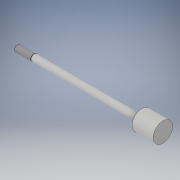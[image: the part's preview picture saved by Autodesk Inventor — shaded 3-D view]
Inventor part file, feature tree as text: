
AUTODESK INVENTOR PART (.ipt)
format: ipt  version: 2019 (Build 230136000, 136)  size: 162,304 bytes
history: native  units: in
note: dims shown in document units (in); Inventor stores cm internally (conversion verified against a paired STEP export)
features: other x70, revolve x3, sketch x3, thread x1
ambient origin geometry x8: Origin, YZ Plane, XZ Plane, XY Plane, X Axis, Y Axis, Z Axis, Center Point
bodies: Solid1 (feature_tree)
feature tree (77):
  revolve  "Revolution1"  Angle=360.0deg
  revolve  "Revolution2"  Angle=360.0deg
  thread  "Thread1"  [1 undecoded]
  revolve  "Revolution3"  [1 undecoded]
  other  "dia1_XY"
  other  "dia1_YZ"
  other  "dia1_ZX"
  other  "dia1_X"
  other  "dia1_Y"
  other  "dia1_Z"
  other  "dia1_Center"
  other  "dia12_XY"
  other  "dia12_YZ"
  other  "dia12_ZX"
  other  "dia12_X"
  other  "dia12_Y"
  other  "dia12_Z"
  other  "dia12_Center"
  other  "dia2_XY"
  other  "dia2_YZ"
  other  "dia2_ZX"
  other  "dia2_X"
  other  "dia2_Y"
  other  "dia2_Z"
  other  "dia2_Center"
  other  "dia22_XY"
  other  "dia22_YZ"
  other  "dia22_ZX"
  other  "dia22_X"
  other  "dia22_Y"
  other  "dia22_Z"
  other  "dia22_Center"
  other  "rl1_XY"
  other  "rl1_YZ"
  other  "rl1_ZX"
  other  "rl1_X"
  other  "rl1_Y"
  other  "rl1_Z"
  other  "rl1_Center"
  other  "rl2_XY"
  other  "rl2_YZ"
  other  "rl2_ZX"
  other  "rl2_X"
  other  "rl2_Y"
  other  "rl2_Z"
  other  "rl2_Center"
  other  "rod_cp_XY"
  other  "rod_cp_YZ"
  other  "rod_cp_ZX"
  other  "rod_cp_X"
  other  "rod_cp_Y"
  other  "rod_cp_Z"
  other  "rod_cp_Center"
  other  "thd1_XY"
  other  "thd1_YZ"
  other  "thd1_ZX"
  other  "thd1_X"
  other  "thd1_Y"
  other  "thd1_Z"
  other  "thd1_Center"
  other  "thd2_XY"
  other  "thd2_YZ"
  other  "thd2_ZX"
  other  "thd2_X"
  other  "thd2_Y"
  other  "thd2_Z"
  other  "thd2_Center"
  other  "to_rod_clevis_XY"
  other  "to_rod_clevis_YZ"
  other  "to_rod_clevis_ZX"
  other  "to_rod_clevis_X"
  other  "to_rod_clevis_Y"
  other  "to_rod_clevis_Z"
  other  "to_rod_clevis_Center"
  sketch  "Sketch_1"  dims[d0=360.0deg d1=360.0deg]
  sketch  "Sketch_3"  dims[d2=0.4814in d3=0.0in d4=360.0deg]
  sketch  "Sketch_30"  dims[d5=0.0in d6=0.0in d7=0.0in d8=0.0in d9=0.0in d10=0.0in]
note: 2 required parameter values undecoded (feature->parameter linkage not recoverable at this tier; creation-order binding heuristic only, values carry confidence <= 0.55)
